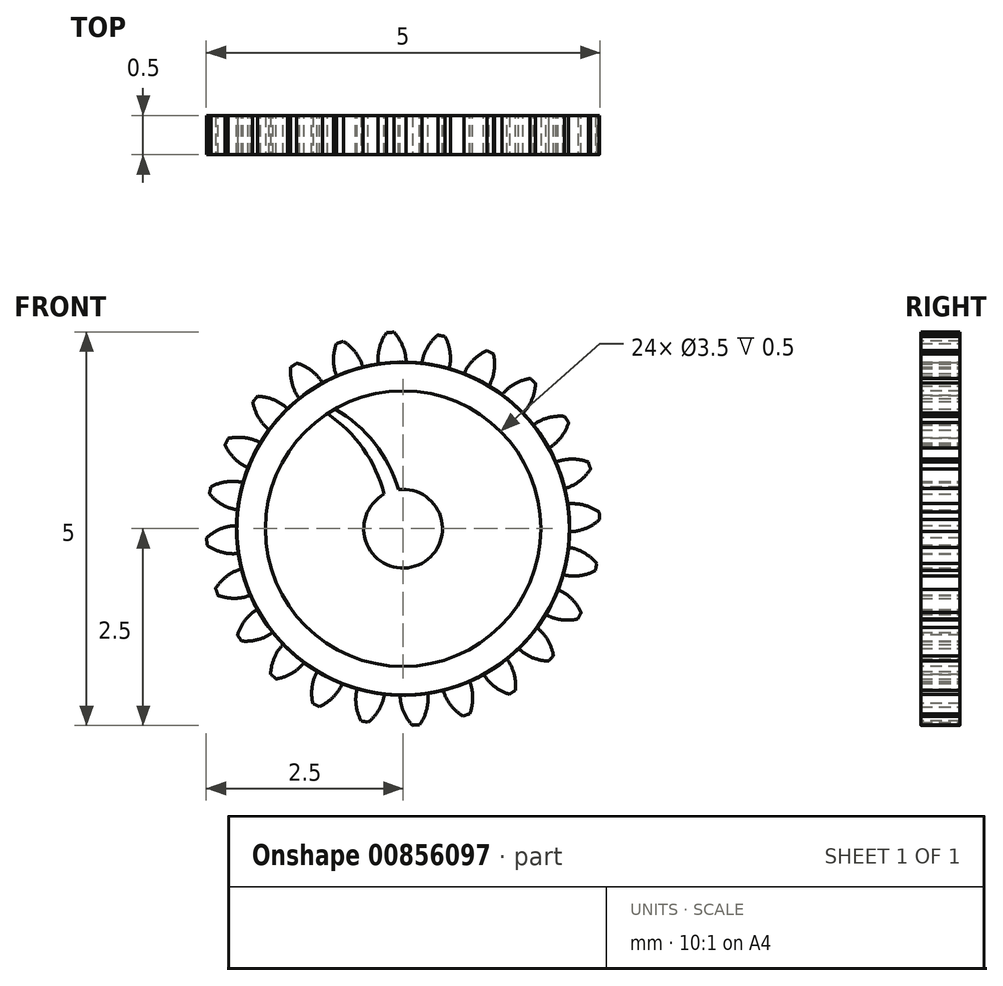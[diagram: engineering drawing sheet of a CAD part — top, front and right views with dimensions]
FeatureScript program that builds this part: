
annotation { "Feature Type Name" : "Feature", "Feature Type Description" : "" }
export const myFeature = defineFeature(function(context is Context, id is Id, definition is map)
    precondition{}
    {
        {
            var Q0;
            Q0=qCreatedBy(makeId("Front.planeOp"),FACE);
            var sketch = newSketch(context, id + "F0", { "sketchPlane" : qUnion([Q0])});
            skCircle(sketch, "E0", {"center": v(0, 0) * mm, "radius": 2.5 * mm, "construction": true});
            skCircle(sketch, "E1", {"center": v(0, 0) * mm, "radius": 2.12 * mm});
            skCircle(sketch, "E2", {"center": v(0, 0) * mm, "radius": 2.31 * mm, "construction": true});
            skLineSegment(sketch, "E3", {"start": v(0, 0) * mm, "end": v(0, 4.06) * mm, "construction": true});
            skLineSegment(sketch, "E4", {"start": v(0, 0) * mm, "end": v(-0.27, 4.06) * mm, "construction": true});
            skLineSegment(sketch, "E5", {"start": v(0, 2.31) * mm, "end": v(-1.69, 2.31) * mm, "construction": true});
            skLineSegment(sketch, "E6", {"start": v(0, 2.31) * mm, "end": v(-1.72, 1.68) * mm, "construction": true});
            skCircle(sketch, "E7", {"center": v(0, 0) * mm, "radius": 2.17 * mm, "construction": true});
            skCircle(sketch, "E8", {"center": v(0, 2.31) * mm, "radius": 0.57 * mm, "construction": true});
            skCircle(sketch, "E9", {"center": v(-0.54, 2.1) * mm, "radius": 0.57 * mm, "construction": true});
            skArc(sketch, "E10", {"start": v(0, 2.31) * mm, "mid": v(-0.05, 2.4) * mm, "end": v(-0.12, 2.5) * mm});
            skArc(sketch, "E11", {"start": v(0.04, 2.11) * mm, "mid": v(0.03, 2.21) * mm, "end": v(0, 2.31) * mm});
            skArc(sketch, "E12.MirrorCS", {"start": v(-0.3, 2.3) * mm, "mid": v(-0.26, 2.4) * mm, "end": v(-0.2, 2.5) * mm});
            skArc(sketch, "E13.MirrorCS", {"start": v(-0.31, 2.1) * mm, "mid": v(-0.32, 2.2) * mm, "end": v(-0.3, 2.3) * mm});
            skArc(sketch, "E14", {"start": v(-0.2, 2.5) * mm, "mid": v(-0.16, 2.5) * mm, "end": v(-0.12, 2.5) * mm});
            skSolve(sketch);
        }
        {
            var Q0;
            {var subQ0=sQuery(id+"F0.wireOp",EDGE,"E1");var subQ1=makeQuery(id+"F0.imprint","INTERSECT",VERTEX,{"derivedFrom":[subQ0,sQuery(id+"F0.wireOp",EDGE,"E11")]});Q0=makeQuery(id+"F0.imprint","IMPRINT",FACE,{"disambiguationData":[TD([[makeQuery(id+"F0.imprint","IMPRINT",EDGE,{"disambiguationData":[TD([[subQ1,-1.0]])],"derivedFrom":subQ0}),1.0]])]});}
            var Q1;
            {var subQ2=sQuery(id+"F0.wireOp",EDGE,"E10");Q1=makeQuery(id+"F0.imprint","IMPRINT",FACE,{"disambiguationData":[TD([[makeQuery(id+"F0.imprint","IMPRINT",EDGE,{"derivedFrom":subQ2}),1.0]])]});}
            extrude(context, id + "F1", {"entities" : qUnion([Q0, Q1]), "depth" : .5 * mm, "offsetDistance" : 25 * mm});
        }
        {
            var Q0;
            Q0=makeQuery(id+"F1.opExtrude","SWEPT_BODY",BODY,{"disambiguationData":[OSD([sQuery(id+"F0.wireOp",EDGE,"E1"),sQuery(id+"F0.wireOp",EDGE,"E10"),sQuery(id+"F0.wireOp",EDGE,"E11"),sQuery(id+"F0.wireOp",EDGE,"E12.MirrorCS"),sQuery(id+"F0.wireOp",EDGE,"E13.MirrorCS"),sQuery(id+"F0.wireOp",EDGE,"E14")])]});
            var Q1;
            Q1=makeQuery(id+"F1.opExtrude","SWEPT_FACE",FACE,{"disambiguationData":[OSD([sQuery(id+"F0.wireOp",EDGE,"E1")])]});
            circularPattern(context, id + "F2", {"entities" : qUnion([Q0]), "axis" : qUnion([Q1]), "angle" : 15 * degree, "instanceCount" : 24});
        }
        {
            var Q0;
            Q0=makeQuery(id+"F1.opExtrude","CAP_FACE",FACE,{"disambiguationData":[OSD([sQuery(id+"F0.wireOp",EDGE,"E1"),sQuery(id+"F0.wireOp",EDGE,"E10"),sQuery(id+"F0.wireOp",EDGE,"E11"),sQuery(id+"F0.wireOp",EDGE,"E12.MirrorCS"),sQuery(id+"F0.wireOp",EDGE,"E13.MirrorCS"),sQuery(id+"F0.wireOp",EDGE,"E14")])],"isStart":false});
            var sketch = newSketch(context, id + "F3", { "sketchPlane" : qUnion([Q0])});
            skCircle(sketch, "E15", {"center": v(0, 0) * mm, "radius": 1.75 * mm});
            skSolve(sketch);
        }
        {
            var Q0;
            Q0=sQuery(id+"F3.wireOp",VERTEX,"E15.center");
            var Q1;
            Q1=makeQuery(id+"F1.opExtrude","SWEPT_BODY",BODY,{"disambiguationData":[OSD([sQuery(id+"F0.wireOp",EDGE,"E1"),sQuery(id+"F0.wireOp",EDGE,"E10"),sQuery(id+"F0.wireOp",EDGE,"E11"),sQuery(id+"F0.wireOp",EDGE,"E12.MirrorCS"),sQuery(id+"F0.wireOp",EDGE,"E13.MirrorCS"),sQuery(id+"F0.wireOp",EDGE,"E14")])]});
            var Q2;
            Q2=makeQuery(id+"F2.opPattern","COPY",BODY,{"derivedFrom":makeQuery(id+"F1.opExtrude","SWEPT_BODY",BODY,{"disambiguationData":[OSD([sQuery(id+"F0.wireOp",EDGE,"E1"),sQuery(id+"F0.wireOp",EDGE,"E10"),sQuery(id+"F0.wireOp",EDGE,"E11"),sQuery(id+"F0.wireOp",EDGE,"E12.MirrorCS"),sQuery(id+"F0.wireOp",EDGE,"E13.MirrorCS"),sQuery(id+"F0.wireOp",EDGE,"E14")])]}),"instanceName":"1"});
            var Q3;
            Q3=makeQuery(id+"F2.opPattern","COPY",BODY,{"derivedFrom":makeQuery(id+"F1.opExtrude","SWEPT_BODY",BODY,{"disambiguationData":[OSD([sQuery(id+"F0.wireOp",EDGE,"E1"),sQuery(id+"F0.wireOp",EDGE,"E10"),sQuery(id+"F0.wireOp",EDGE,"E11"),sQuery(id+"F0.wireOp",EDGE,"E12.MirrorCS"),sQuery(id+"F0.wireOp",EDGE,"E13.MirrorCS"),sQuery(id+"F0.wireOp",EDGE,"E14")])]}),"instanceName":"2"});
            var Q4;
            Q4=makeQuery(id+"F2.opPattern","COPY",BODY,{"derivedFrom":makeQuery(id+"F1.opExtrude","SWEPT_BODY",BODY,{"disambiguationData":[OSD([sQuery(id+"F0.wireOp",EDGE,"E1"),sQuery(id+"F0.wireOp",EDGE,"E10"),sQuery(id+"F0.wireOp",EDGE,"E11"),sQuery(id+"F0.wireOp",EDGE,"E12.MirrorCS"),sQuery(id+"F0.wireOp",EDGE,"E13.MirrorCS"),sQuery(id+"F0.wireOp",EDGE,"E14")])]}),"instanceName":"3"});
            var Q5;
            Q5=makeQuery(id+"F2.opPattern","COPY",BODY,{"derivedFrom":makeQuery(id+"F1.opExtrude","SWEPT_BODY",BODY,{"disambiguationData":[OSD([sQuery(id+"F0.wireOp",EDGE,"E1"),sQuery(id+"F0.wireOp",EDGE,"E10"),sQuery(id+"F0.wireOp",EDGE,"E11"),sQuery(id+"F0.wireOp",EDGE,"E12.MirrorCS"),sQuery(id+"F0.wireOp",EDGE,"E13.MirrorCS"),sQuery(id+"F0.wireOp",EDGE,"E14")])]}),"instanceName":"4"});
            var Q6;
            Q6=makeQuery(id+"F2.opPattern","COPY",BODY,{"derivedFrom":makeQuery(id+"F1.opExtrude","SWEPT_BODY",BODY,{"disambiguationData":[OSD([sQuery(id+"F0.wireOp",EDGE,"E1"),sQuery(id+"F0.wireOp",EDGE,"E10"),sQuery(id+"F0.wireOp",EDGE,"E11"),sQuery(id+"F0.wireOp",EDGE,"E12.MirrorCS"),sQuery(id+"F0.wireOp",EDGE,"E13.MirrorCS"),sQuery(id+"F0.wireOp",EDGE,"E14")])]}),"instanceName":"5"});
            var Q7;
            Q7=makeQuery(id+"F2.opPattern","COPY",BODY,{"derivedFrom":makeQuery(id+"F1.opExtrude","SWEPT_BODY",BODY,{"disambiguationData":[OSD([sQuery(id+"F0.wireOp",EDGE,"E1"),sQuery(id+"F0.wireOp",EDGE,"E10"),sQuery(id+"F0.wireOp",EDGE,"E11"),sQuery(id+"F0.wireOp",EDGE,"E12.MirrorCS"),sQuery(id+"F0.wireOp",EDGE,"E13.MirrorCS"),sQuery(id+"F0.wireOp",EDGE,"E14")])]}),"instanceName":"6"});
            var Q8;
            Q8=makeQuery(id+"F2.opPattern","COPY",BODY,{"derivedFrom":makeQuery(id+"F1.opExtrude","SWEPT_BODY",BODY,{"disambiguationData":[OSD([sQuery(id+"F0.wireOp",EDGE,"E1"),sQuery(id+"F0.wireOp",EDGE,"E10"),sQuery(id+"F0.wireOp",EDGE,"E11"),sQuery(id+"F0.wireOp",EDGE,"E12.MirrorCS"),sQuery(id+"F0.wireOp",EDGE,"E13.MirrorCS"),sQuery(id+"F0.wireOp",EDGE,"E14")])]}),"instanceName":"7"});
            var Q9;
            Q9=makeQuery(id+"F2.opPattern","COPY",BODY,{"derivedFrom":makeQuery(id+"F1.opExtrude","SWEPT_BODY",BODY,{"disambiguationData":[OSD([sQuery(id+"F0.wireOp",EDGE,"E1"),sQuery(id+"F0.wireOp",EDGE,"E10"),sQuery(id+"F0.wireOp",EDGE,"E11"),sQuery(id+"F0.wireOp",EDGE,"E12.MirrorCS"),sQuery(id+"F0.wireOp",EDGE,"E13.MirrorCS"),sQuery(id+"F0.wireOp",EDGE,"E14")])]}),"instanceName":"8"});
            var Q10;
            Q10=makeQuery(id+"F2.opPattern","COPY",BODY,{"derivedFrom":makeQuery(id+"F1.opExtrude","SWEPT_BODY",BODY,{"disambiguationData":[OSD([sQuery(id+"F0.wireOp",EDGE,"E1"),sQuery(id+"F0.wireOp",EDGE,"E10"),sQuery(id+"F0.wireOp",EDGE,"E11"),sQuery(id+"F0.wireOp",EDGE,"E12.MirrorCS"),sQuery(id+"F0.wireOp",EDGE,"E13.MirrorCS"),sQuery(id+"F0.wireOp",EDGE,"E14")])]}),"instanceName":"9"});
            var Q11;
            Q11=makeQuery(id+"F2.opPattern","COPY",BODY,{"derivedFrom":makeQuery(id+"F1.opExtrude","SWEPT_BODY",BODY,{"disambiguationData":[OSD([sQuery(id+"F0.wireOp",EDGE,"E1"),sQuery(id+"F0.wireOp",EDGE,"E10"),sQuery(id+"F0.wireOp",EDGE,"E11"),sQuery(id+"F0.wireOp",EDGE,"E12.MirrorCS"),sQuery(id+"F0.wireOp",EDGE,"E13.MirrorCS"),sQuery(id+"F0.wireOp",EDGE,"E14")])]}),"instanceName":"10"});
            var Q12;
            Q12=makeQuery(id+"F2.opPattern","COPY",BODY,{"derivedFrom":makeQuery(id+"F1.opExtrude","SWEPT_BODY",BODY,{"disambiguationData":[OSD([sQuery(id+"F0.wireOp",EDGE,"E1"),sQuery(id+"F0.wireOp",EDGE,"E10"),sQuery(id+"F0.wireOp",EDGE,"E11"),sQuery(id+"F0.wireOp",EDGE,"E12.MirrorCS"),sQuery(id+"F0.wireOp",EDGE,"E13.MirrorCS"),sQuery(id+"F0.wireOp",EDGE,"E14")])]}),"instanceName":"11"});
            var Q13;
            Q13=makeQuery(id+"F2.opPattern","COPY",BODY,{"derivedFrom":makeQuery(id+"F1.opExtrude","SWEPT_BODY",BODY,{"disambiguationData":[OSD([sQuery(id+"F0.wireOp",EDGE,"E1"),sQuery(id+"F0.wireOp",EDGE,"E10"),sQuery(id+"F0.wireOp",EDGE,"E11"),sQuery(id+"F0.wireOp",EDGE,"E12.MirrorCS"),sQuery(id+"F0.wireOp",EDGE,"E13.MirrorCS"),sQuery(id+"F0.wireOp",EDGE,"E14")])]}),"instanceName":"12"});
            var Q14;
            Q14=makeQuery(id+"F2.opPattern","COPY",BODY,{"derivedFrom":makeQuery(id+"F1.opExtrude","SWEPT_BODY",BODY,{"disambiguationData":[OSD([sQuery(id+"F0.wireOp",EDGE,"E1"),sQuery(id+"F0.wireOp",EDGE,"E10"),sQuery(id+"F0.wireOp",EDGE,"E11"),sQuery(id+"F0.wireOp",EDGE,"E12.MirrorCS"),sQuery(id+"F0.wireOp",EDGE,"E13.MirrorCS"),sQuery(id+"F0.wireOp",EDGE,"E14")])]}),"instanceName":"13"});
            var Q15;
            Q15=makeQuery(id+"F2.opPattern","COPY",BODY,{"derivedFrom":makeQuery(id+"F1.opExtrude","SWEPT_BODY",BODY,{"disambiguationData":[OSD([sQuery(id+"F0.wireOp",EDGE,"E1"),sQuery(id+"F0.wireOp",EDGE,"E10"),sQuery(id+"F0.wireOp",EDGE,"E11"),sQuery(id+"F0.wireOp",EDGE,"E12.MirrorCS"),sQuery(id+"F0.wireOp",EDGE,"E13.MirrorCS"),sQuery(id+"F0.wireOp",EDGE,"E14")])]}),"instanceName":"14"});
            var Q16;
            Q16=makeQuery(id+"F2.opPattern","COPY",BODY,{"derivedFrom":makeQuery(id+"F1.opExtrude","SWEPT_BODY",BODY,{"disambiguationData":[OSD([sQuery(id+"F0.wireOp",EDGE,"E1"),sQuery(id+"F0.wireOp",EDGE,"E10"),sQuery(id+"F0.wireOp",EDGE,"E11"),sQuery(id+"F0.wireOp",EDGE,"E12.MirrorCS"),sQuery(id+"F0.wireOp",EDGE,"E13.MirrorCS"),sQuery(id+"F0.wireOp",EDGE,"E14")])]}),"instanceName":"15"});
            var Q17;
            Q17=makeQuery(id+"F2.opPattern","COPY",BODY,{"derivedFrom":makeQuery(id+"F1.opExtrude","SWEPT_BODY",BODY,{"disambiguationData":[OSD([sQuery(id+"F0.wireOp",EDGE,"E1"),sQuery(id+"F0.wireOp",EDGE,"E10"),sQuery(id+"F0.wireOp",EDGE,"E11"),sQuery(id+"F0.wireOp",EDGE,"E12.MirrorCS"),sQuery(id+"F0.wireOp",EDGE,"E13.MirrorCS"),sQuery(id+"F0.wireOp",EDGE,"E14")])]}),"instanceName":"16"});
            var Q18;
            Q18=makeQuery(id+"F2.opPattern","COPY",BODY,{"derivedFrom":makeQuery(id+"F1.opExtrude","SWEPT_BODY",BODY,{"disambiguationData":[OSD([sQuery(id+"F0.wireOp",EDGE,"E1"),sQuery(id+"F0.wireOp",EDGE,"E10"),sQuery(id+"F0.wireOp",EDGE,"E11"),sQuery(id+"F0.wireOp",EDGE,"E12.MirrorCS"),sQuery(id+"F0.wireOp",EDGE,"E13.MirrorCS"),sQuery(id+"F0.wireOp",EDGE,"E14")])]}),"instanceName":"17"});
            var Q19;
            Q19=makeQuery(id+"F2.opPattern","COPY",BODY,{"derivedFrom":makeQuery(id+"F1.opExtrude","SWEPT_BODY",BODY,{"disambiguationData":[OSD([sQuery(id+"F0.wireOp",EDGE,"E1"),sQuery(id+"F0.wireOp",EDGE,"E10"),sQuery(id+"F0.wireOp",EDGE,"E11"),sQuery(id+"F0.wireOp",EDGE,"E12.MirrorCS"),sQuery(id+"F0.wireOp",EDGE,"E13.MirrorCS"),sQuery(id+"F0.wireOp",EDGE,"E14")])]}),"instanceName":"18"});
            var Q20;
            Q20=makeQuery(id+"F2.opPattern","COPY",BODY,{"derivedFrom":makeQuery(id+"F1.opExtrude","SWEPT_BODY",BODY,{"disambiguationData":[OSD([sQuery(id+"F0.wireOp",EDGE,"E1"),sQuery(id+"F0.wireOp",EDGE,"E10"),sQuery(id+"F0.wireOp",EDGE,"E11"),sQuery(id+"F0.wireOp",EDGE,"E12.MirrorCS"),sQuery(id+"F0.wireOp",EDGE,"E13.MirrorCS"),sQuery(id+"F0.wireOp",EDGE,"E14")])]}),"instanceName":"19"});
            var Q21;
            Q21=makeQuery(id+"F2.opPattern","COPY",BODY,{"derivedFrom":makeQuery(id+"F1.opExtrude","SWEPT_BODY",BODY,{"disambiguationData":[OSD([sQuery(id+"F0.wireOp",EDGE,"E1"),sQuery(id+"F0.wireOp",EDGE,"E10"),sQuery(id+"F0.wireOp",EDGE,"E11"),sQuery(id+"F0.wireOp",EDGE,"E12.MirrorCS"),sQuery(id+"F0.wireOp",EDGE,"E13.MirrorCS"),sQuery(id+"F0.wireOp",EDGE,"E14")])]}),"instanceName":"20"});
            var Q22;
            Q22=makeQuery(id+"F2.opPattern","COPY",BODY,{"derivedFrom":makeQuery(id+"F1.opExtrude","SWEPT_BODY",BODY,{"disambiguationData":[OSD([sQuery(id+"F0.wireOp",EDGE,"E1"),sQuery(id+"F0.wireOp",EDGE,"E10"),sQuery(id+"F0.wireOp",EDGE,"E11"),sQuery(id+"F0.wireOp",EDGE,"E12.MirrorCS"),sQuery(id+"F0.wireOp",EDGE,"E13.MirrorCS"),sQuery(id+"F0.wireOp",EDGE,"E14")])]}),"instanceName":"21"});
            var Q23;
            Q23=makeQuery(id+"F2.opPattern","COPY",BODY,{"derivedFrom":makeQuery(id+"F1.opExtrude","SWEPT_BODY",BODY,{"disambiguationData":[OSD([sQuery(id+"F0.wireOp",EDGE,"E1"),sQuery(id+"F0.wireOp",EDGE,"E10"),sQuery(id+"F0.wireOp",EDGE,"E11"),sQuery(id+"F0.wireOp",EDGE,"E12.MirrorCS"),sQuery(id+"F0.wireOp",EDGE,"E13.MirrorCS"),sQuery(id+"F0.wireOp",EDGE,"E14")])]}),"instanceName":"22"});
            var Q24;
            Q24=makeQuery(id+"F2.opPattern","COPY",BODY,{"derivedFrom":makeQuery(id+"F1.opExtrude","SWEPT_BODY",BODY,{"disambiguationData":[OSD([sQuery(id+"F0.wireOp",EDGE,"E1"),sQuery(id+"F0.wireOp",EDGE,"E10"),sQuery(id+"F0.wireOp",EDGE,"E11"),sQuery(id+"F0.wireOp",EDGE,"E12.MirrorCS"),sQuery(id+"F0.wireOp",EDGE,"E13.MirrorCS"),sQuery(id+"F0.wireOp",EDGE,"E14")])]}),"instanceName":"23"});
            hole(context, id + "F4", {"style" : HoleStyle.SIMPLE, "endStyle" : HoleEndStyle.THROUGH, "holeDiameter" : 3.5 * mm, "majorDiameter" : 5 * mm, "isTappedThrough" : true, "tappedDepth" : 12 * mm, "tapClearance" : 3, "startFromSketch" : true, "locations" : qUnion([Q0]), "scope" : qUnion([Q1, Q2, Q3, Q4, Q5, Q6, Q7, Q8, Q9, Q10, Q11, Q12, Q13, Q14, Q15, Q16, Q17, Q18, Q19, Q20, Q21, Q22, Q23, Q24])});
        }
        {
            var Q0;
            Q0=qCreatedBy(makeId("Front.planeOp"),FACE);
            var sketch = newSketch(context, id + "F5", { "sketchPlane" : qUnion([Q0])});
            skCircle(sketch, "E16", {"center": v(0, 0) * mm, "radius": 0.5 * mm});
            skSolve(sketch);
        }
        {
            var Q0;
            Q0=makeQuery(id+"F5.imprint","IMPRINT",FACE,{"disambiguationData":[TD([[makeQuery(id+"F5.imprint","IMPRINT",EDGE,{"derivedFrom":sQuery(id+"F5.wireOp",EDGE,"E16")}),1.0]])]});
            extrude(context, id + "F6", {"entities" : qUnion([Q0]), "depth" : 0.5 * mm, "offsetDistance" : 25 * mm});
        }
        {
            var Q0;
            Q0=qCreatedBy(makeId("Front.planeOp"),FACE);
            var sketch = newSketch(context, id + "F7", { "sketchPlane" : qUnion([Q0])});
            skArc(sketch, "E17", {"start": v(-0.06, 0.5) * mm, "mid": v(-0.36, 1.09) * mm, "end": v(-0.86, 1.52) * mm});
            skArc(sketch, "E18", {"start": v(-0.86, 1.52) * mm, "mid": v(-3.13, -1.09) * mm, "end": v(-0.06, 0.5) * mm, "construction": true});
            skArc(sketch, "E19", {"start": v(-0.24, 0.44) * mm, "mid": v(-0.5, 1.02) * mm, "end": v(-0.96, 1.46) * mm});
            skArc(sketch, "E20", {"start": v(-0.96, 1.46) * mm, "mid": v(-3.38, -1.02) * mm, "end": v(-0.24, 0.44) * mm, "construction": true});
            skArc(sketch, "E21", {"start": v(-0.06, 0.5) * mm, "mid": v(-0.15, 0.48) * mm, "end": v(-0.24, 0.44) * mm});
            skArc(sketch, "E22", {"start": v(-0.86, 1.52) * mm, "mid": v(-0.91, 1.5) * mm, "end": v(-0.96, 1.46) * mm});
            skSolve(sketch);
        }
        {
            var Q0;
            Q0=makeQuery(id+"F7.imprint","IMPRINT",FACE,{"disambiguationData":[TD([[makeQuery(id+"F7.imprint","IMPRINT",EDGE,{"derivedFrom":sQuery(id+"F7.wireOp",EDGE,"E17")}),1.0]])]});
            extrude(context, id + "F8", {"entities" : qUnion([Q0]), "operationType" : NewBodyOperationType.ADD, "depth" : .5 * mm, "offsetDistance" : 25 * mm});
        }
    });
